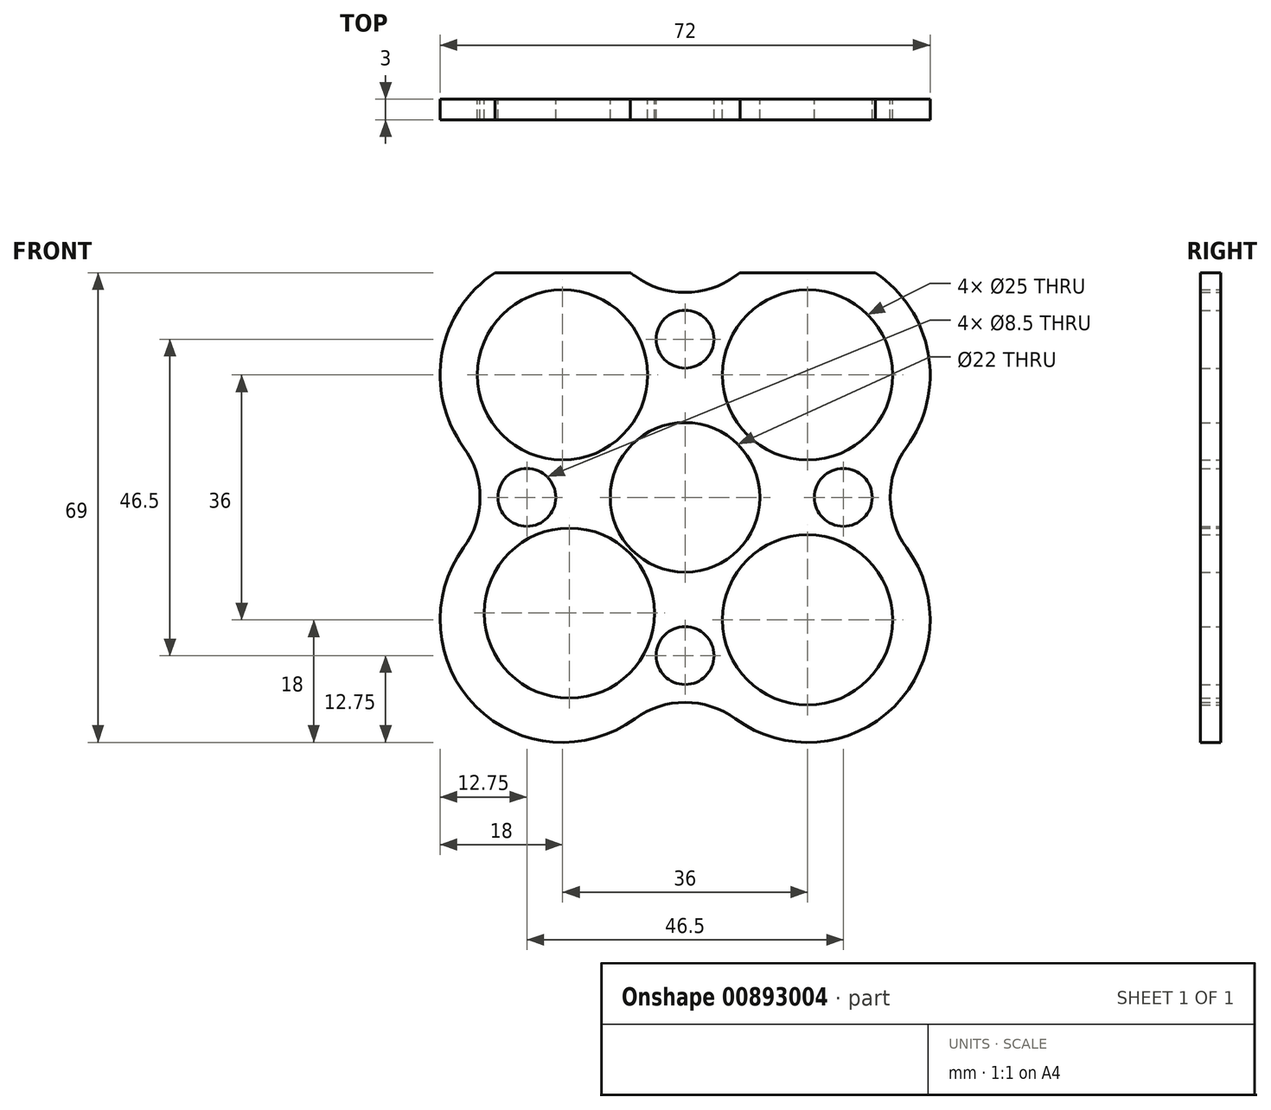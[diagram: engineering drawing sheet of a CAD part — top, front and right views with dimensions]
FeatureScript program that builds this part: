
annotation { "Feature Type Name" : "Feature", "Feature Type Description" : "" }
export const myFeature = defineFeature(function(context is Context, id is Id, definition is map)
    precondition{}
    {
        {
            var Q0;
            Q0=qCreatedBy(makeId("Front.planeOp"),FACE);
            var sketch = newSketch(context, id + "F0", { "sketchPlane" : qUnion([Q0])});
            skCircle(sketch, "E0", {"center": v(0, 0) * mm, "radius": 11 * mm});
            skCircle(sketch, "E1", {"center": v(-18, 18) * mm, "radius": 12.5 * mm});
            skCircle(sketch, "E2", {"center": v(18, 18) * mm, "radius": 12.5 * mm});
            skLineSegment(sketch, "E3", {"start": v(18, 18) * mm, "end": v(18, 49.18) * mm, "construction": true});
            skLineSegment(sketch, "E4", {"start": v(-18, 18) * mm, "end": v(-18, 49.78) * mm, "construction": true});
            skArc(sketch, "E5", {"start": v(32.53, 7.38) * mm, "mid": v(35.72, 21.17) * mm, "end": v(27.95, 33) * mm});
            skArc(sketch, "E6", {"start": v(-7.38, 32.53) * mm, "mid": v(-7.71, 32.77) * mm, "end": v(-8.05, 33) * mm});
            skCircle(sketch, "E7", {"center": v(18, -18) * mm, "radius": 12.5 * mm});
            skArc(sketch, "E8", {"start": v(7.38, -32.53) * mm, "mid": v(30.73, -30.73) * mm, "end": v(32.53, -7.38) * mm});
            skArc(sketch, "E9", {"start": v(-32.53, -7.38) * mm, "mid": v(-30.73, -30.73) * mm, "end": v(-7.38, -32.53) * mm});
            skPoint(sketch, "E10.visualSharp", {"position": v(0, 18) * mm});
            skArc(sketch, "E10.filletArc", {"start": v(-7.38, 32.53) * mm, "mid": v(0, 30.12) * mm, "end": v(7.38, 32.53) * mm});
            skPoint(sketch, "E11.visualSharp", {"position": v(18, 0) * mm});
            skArc(sketch, "E11.filletArc", {"start": v(32.53, 7.38) * mm, "mid": v(30.12, 0) * mm, "end": v(32.53, -7.38) * mm});
            skPoint(sketch, "E12.visualSharp", {"position": v(0, -18) * mm});
            skArc(sketch, "E12.filletArc", {"start": v(7.38, -32.53) * mm, "mid": v(0, -30.12) * mm, "end": v(-7.38, -32.53) * mm});
            skPoint(sketch, "E13.visualSharp", {"position": v(-18, 0) * mm});
            skArc(sketch, "E13.filletArc", {"start": v(-32.53, -7.38) * mm, "mid": v(-30.12, 0) * mm, "end": v(-32.53, 7.38) * mm});
            skCircle(sketch, "E14", {"center": v(0, 23.25) * mm, "radius": 4.25 * mm});
            skCircle(sketch, "E15", {"center": v(-23.25, 0) * mm, "radius": 4.25 * mm});
            skCircle(sketch, "E16", {"center": v(23.25, 0) * mm, "radius": 4.25 * mm});
            skCircle(sketch, "E17", {"center": v(0, -23.25) * mm, "radius": 4.25 * mm});
            skLineSegment(sketch, "E18", {"start": v(-27.95, 33) * mm, "end": v(-8.05, 33) * mm});
            skLineSegment(sketch, "E19.trimOffspring", {"start": v(8.05, 33) * mm, "end": v(27.95, 33) * mm});
            skArc(sketch, "E20.trimOffspring", {"start": v(8.05, 33) * mm, "mid": v(7.71, 32.77) * mm, "end": v(7.38, 32.53) * mm});
            skArc(sketch, "E21.trimOffspring", {"start": v(-27.95, 33) * mm, "mid": v(-35.72, 21.17) * mm, "end": v(-32.53, 7.38) * mm});
            skCircle(sketch, "E22", {"center": v(-17, -17) * mm, "radius": 12.5 * mm});
            skSolve(sketch);
        }
        {
            var Q0;
            Q0=makeQuery(id+"F0.imprint","IMPRINT",FACE,{"disambiguationData":[TD([[makeQuery(id+"F0.imprint","IMPRINT",EDGE,{"derivedFrom":sQuery(id+"F0.wireOp",EDGE,"E0")}),-1.0]])]});
            extrude(context, id + "F1", {"entities" : qUnion([Q0]), "depth" : 3 * mm, "offsetDistance" : 25 * mm});
        }
    });
